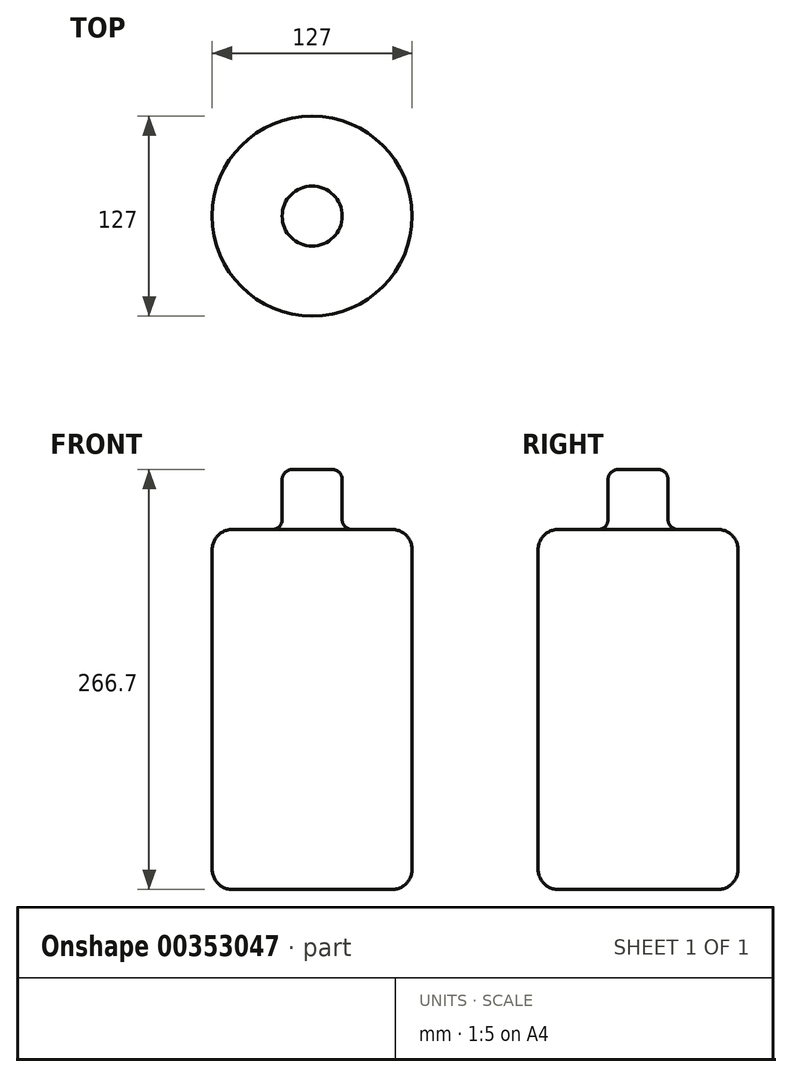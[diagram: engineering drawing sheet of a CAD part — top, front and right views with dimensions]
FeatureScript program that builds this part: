
annotation { "Feature Type Name" : "Feature", "Feature Type Description" : "" }
export const myFeature = defineFeature(function(context is Context, id is Id, definition is map)
    precondition{}
    {
        {
            var Q0;
            Q0=qCreatedBy(makeId("Front.planeOp"),FACE);
            var sketch = newSketch(context, id + "F0", { "sketchPlane" : qUnion([Q0])});
            skLineSegment(sketch, "E0.bottom", {"start": v(-69.85, 100.11) * mm, "end": v(31.75, 100.11) * mm});
            skLineSegment(sketch, "E0.top", {"start": v(-69.85, -128.49) * mm, "end": v(31.75, -128.49) * mm});
            skLineSegment(sketch, "E0.left", {"start": v(-82.55, 87.41) * mm, "end": v(-82.55, -115.79) * mm});
            skLineSegment(sketch, "E0.right", {"start": v(44.45, 87.41) * mm, "end": v(44.45, -115.79) * mm});
            skPoint(sketch, "E1.visualSharp", {"position": v(-82.55, 100.11) * mm});
            skArc(sketch, "E1.filletArc", {"start": v(-69.85, 100.11) * mm, "mid": v(-78.83, 96.4) * mm, "end": v(-82.55, 87.41) * mm});
            skPoint(sketch, "E2.visualSharp", {"position": v(44.45, 100.11) * mm});
            skArc(sketch, "E2.filletArc", {"start": v(44.45, 87.41) * mm, "mid": v(40.73, 96.4) * mm, "end": v(31.75, 100.11) * mm});
            skPoint(sketch, "E3.visualSharp", {"position": v(-82.55, -128.49) * mm});
            skArc(sketch, "E3.filletArc", {"start": v(-82.55, -115.79) * mm, "mid": v(-78.83, -124.77) * mm, "end": v(-69.85, -128.49) * mm});
            skPoint(sketch, "E4.visualSharp", {"position": v(44.45, -128.49) * mm});
            skArc(sketch, "E4.filletArc", {"start": v(31.75, -128.49) * mm, "mid": v(40.73, -124.77) * mm, "end": v(44.45, -115.79) * mm});
            skLineSegment(sketch, "E5.bottom", {"start": v(-38.1, 100.11) * mm, "end": v(0, 100.11) * mm});
            skLineSegment(sketch, "E5.top", {"start": v(-38.1, 138.21) * mm, "end": v(0, 138.21) * mm});
            skLineSegment(sketch, "E5.left", {"start": v(-38.1, 100.11) * mm, "end": v(-38.1, 138.21) * mm});
            skLineSegment(sketch, "E5.right", {"start": v(0, 100.11) * mm, "end": v(0, 138.21) * mm});
            skLineSegment(sketch, "E6", {"start": v(-19.05, 167.65) * mm, "end": v(-19.05, -145.2) * mm});
            skSolve(sketch);
        }
        {
            var Q0;
            Q0=makeQuery(id+"F0.imprint","IMPRINT",FACE,{"disambiguationData":[TD([[makeQuery(id+"F0.imprint","IMPRINT",EDGE,{"derivedFrom":sQuery(id+"F0.wireOp",EDGE,"E0.left")}),1.0]])]});
            var Q1;
            {var subQ0=sQuery(id+"F0.wireOp",EDGE,"E5.left");Q1=makeQuery(id+"F0.imprint","IMPRINT",FACE,{"disambiguationData":[TD([[makeQuery(id+"F0.imprint","IMPRINT",EDGE,{"derivedFrom":subQ0}),-1.0]])]});}
            var Q2;
            Q2=sQuery(id+"F0.wireOp",EDGE,"E6");
            revolve(context, id + "F1", {"entities" : qUnion([Q0, Q1]), "axis" : qUnion([Q2]), "revolveType" : RevolveType.FULL});
        }
        {
            var Q0;
            Q0=makeQuery(id+"F1.opRevolve","SWEPT_EDGE",EDGE,{"disambiguationData":[OSD([sQuery(id+"F0.wireOp",EDGE,"E0.bottom"),sQuery(id+"F0.wireOp",EDGE,"E5.bottom"),sQuery(id+"F0.wireOp",EDGE,"E5.left")])]});
            var Q1;
            Q1=makeQuery(id+"F1.opRevolve","SWEPT_EDGE",EDGE,{"disambiguationData":[OSD([sQuery(id+"F0.wireOp",EDGE,"E5.top"),sQuery(id+"F0.wireOp",EDGE,"E5.left")])]});
            fillet(context, id + "F2", {"entities" : qUnion([Q0, Q1]), "radius" : 6.35 * mm, "tangentPropagation" : true, "allowEdgeOverflow" : false});
        }
    });
